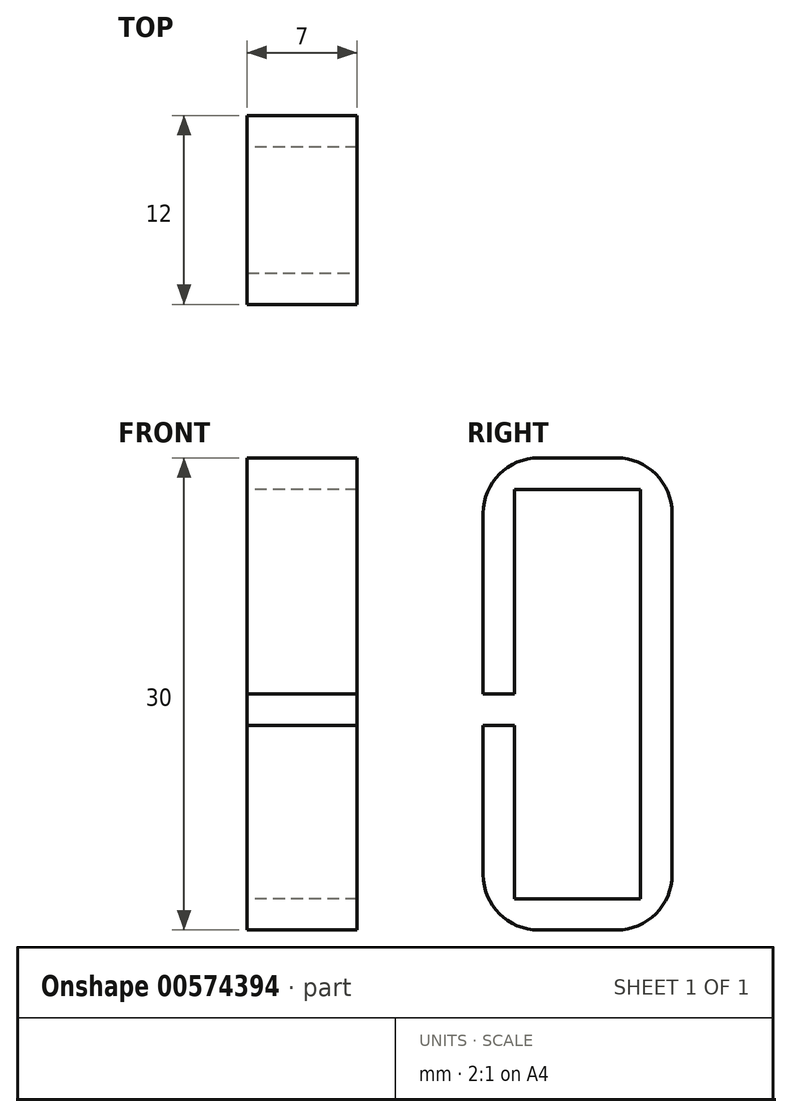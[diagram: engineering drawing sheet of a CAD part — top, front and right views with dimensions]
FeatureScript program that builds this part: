
annotation { "Feature Type Name" : "Feature", "Feature Type Description" : "" }
export const myFeature = defineFeature(function(context is Context, id is Id, definition is map)
    precondition{}
    {
        {
            var Q0;
            Q0=qCreatedBy(makeId("Front.planeOp"),FACE);
            var sketch = newSketch(context, id + "F0", { "sketchPlane" : qUnion([Q0])});
            skLineSegment(sketch, "E0.bottom", {"start": v(0, 0) * mm, "end": v(-7, 0) * mm});
            skLineSegment(sketch, "E0.top", {"start": v(0, 26) * mm, "end": v(-7, 26) * mm});
            skLineSegment(sketch, "E0.left", {"start": v(0, 0) * mm, "end": v(0, 26) * mm});
            skLineSegment(sketch, "E0.right", {"start": v(-7, 0) * mm, "end": v(-7, 26) * mm});
            skSolve(sketch);
        }
        {
            var Q0;
            Q0 = qSketchRegion(id + "F0", true);
            extrude(context, id + "F1", {"entities" : qUnion([Q0]), "depth" : 2 * mm, "offsetDistance" : 25.4 * mm});
        }
        {
            var Q0;
            Q0 = qSketchRegion(id + "F0", true);
            extrude(context, id + "F2", {"entities" : qUnion([Q0]), "depth" : 12 * mm, "offsetDistance" : 25.4 * mm, "hasSecondDirection" : true, "secondDirectionOppositeDirection" : false, "secondDirectionDepth" : 10 * mm});
        }
        {
            var Q0;
            Q0=makeQuery(id+"F1.opExtrude","SWEPT_FACE",FACE,{"disambiguationData":[OSD([sQuery(id+"F0.wireOp",EDGE,"E0.top")])]});
            var sketch = newSketch(context, id + "F3", { "sketchPlane" : qUnion([Q0])});
            skLineSegment(sketch, "E1.bottom", {"start": v(0, 0) * mm, "end": v(-7, 0) * mm});
            skLineSegment(sketch, "E1.top", {"start": v(0, -12) * mm, "end": v(-7, -12) * mm});
            skLineSegment(sketch, "E1.left", {"start": v(0, 0) * mm, "end": v(0, -12) * mm});
            skLineSegment(sketch, "E1.right", {"start": v(-7, 0) * mm, "end": v(-7, -12) * mm});
            skSolve(sketch);
        }
        {
            var Q0;
            Q0 = qSketchRegion(id + "F3", true);
            extrude(context, id + "F4", {"entities" : qUnion([Q0]), "depth" : 2 * mm, "offsetDistance" : 25.4 * mm});
        }
        {
            var Q0;
            Q0 = qSketchRegion(id + "F3", true);
            extrude(context, id + "F5", {"entities" : qUnion([Q0]), "oppositeDirection" : true, "depth" : 28 * mm, "offsetDistance" : 25.4 * mm, "hasSecondDirection" : true, "secondDirectionOppositeDirection" : true, "secondDirectionDepth" : 26 * mm});
        }
        {
            var Q0;
            Q0=makeQuery(id+"F1.opExtrude","SWEPT_BODY",BODY,{"disambiguationData":[OSD([sQuery(id+"F0.wireOp",EDGE,"E0.bottom"),sQuery(id+"F0.wireOp",EDGE,"E0.top"),sQuery(id+"F0.wireOp",EDGE,"E0.left"),sQuery(id+"F0.wireOp",EDGE,"E0.right")])]});
            var Q1;
            Q1=makeQuery(id+"F2.opExtrude","SWEPT_BODY",BODY,{"disambiguationData":[OSD([sQuery(id+"F0.wireOp",EDGE,"E0.bottom"),sQuery(id+"F0.wireOp",EDGE,"E0.top"),sQuery(id+"F0.wireOp",EDGE,"E0.left"),sQuery(id+"F0.wireOp",EDGE,"E0.right")])]});
            var Q2;
            Q2=makeQuery(id+"F4.opExtrude","SWEPT_BODY",BODY,{"disambiguationData":[OSD([sQuery(id+"F3.wireOp",EDGE,"E1.bottom"),sQuery(id+"F3.wireOp",EDGE,"E1.top"),sQuery(id+"F3.wireOp",EDGE,"E1.left"),sQuery(id+"F3.wireOp",EDGE,"E1.right")])]});
            var Q3;
            Q3=makeQuery(id+"F5.opExtrude","SWEPT_BODY",BODY,{"disambiguationData":[OSD([sQuery(id+"F3.wireOp",EDGE,"E1.bottom"),sQuery(id+"F3.wireOp",EDGE,"E1.top"),sQuery(id+"F3.wireOp",EDGE,"E1.left"),sQuery(id+"F3.wireOp",EDGE,"E1.right")])]});
            booleanBodies(context, id + "F6", {"operationType" : BooleanOperationType.UNION, "tools" : qUnion([Q0, Q1, Q2, Q3])});
        }
        {
            var Q0;
            {var subQ0=sQuery(id+"F3.wireOp",EDGE,"E1.top");Q0=makeQuery(id+"F6.opBoolean","MERGE",FACE,{"derivedFrom":[makeQuery(id+"F2.opExtrude","CAP_FACE",FACE,{"disambiguationData":[OSD([sQuery(id+"F0.wireOp",EDGE,"E0.bottom"),sQuery(id+"F0.wireOp",EDGE,"E0.top"),sQuery(id+"F0.wireOp",EDGE,"E0.left"),sQuery(id+"F0.wireOp",EDGE,"E0.right")])],"isStart":false}),makeQuery(id+"F4.opExtrude","SWEPT_FACE",FACE,{"disambiguationData":[OSD([subQ0])]}),makeQuery(id+"F5.opExtrude","SWEPT_FACE",FACE,{"disambiguationData":[OSD([subQ0])]})]});}
            var sketch = newSketch(context, id + "F7", { "sketchPlane" : qUnion([Q0])});
            skLineSegment(sketch, "E2", {"start": v(-7, 13) * mm, "end": v(0, 13) * mm});
            skLineSegment(sketch, "E3.top", {"start": v(-7, 11) * mm, "end": v(0, 11) * mm});
            skSolve(sketch);
        }
        {
            var Q0;
            {var subQ0=sQuery(id+"F7.wireOp",EDGE,"E2");Q0=makeQuery(id+"F7.imprint","IMPRINT",FACE,{"disambiguationData":[TD([[makeQuery(id+"F7.imprint","IMPRINT",EDGE,{"derivedFrom":subQ0}),-1.0]])]});}
            extrude(context, id + "F8", {"entities" : qUnion([Q0]), "operationType" : NewBodyOperationType.REMOVE, "oppositeDirection" : true, "depth" : 4 * mm, "offsetDistance" : 25.4 * mm});
        }
        {
            var Q0;
            Q0=makeQuery(id+"F4.opExtrude","CAP_EDGE",EDGE,{"disambiguationData":[OSD([sQuery(id+"F3.wireOp",EDGE,"E1.top")])],"isStart":false});
            var Q1;
            Q1=makeQuery(id+"F4.opExtrude","CAP_EDGE",EDGE,{"disambiguationData":[OSD([sQuery(id+"F3.wireOp",EDGE,"E1.bottom")])],"isStart":false});
            var Q2;
            Q2=makeQuery(id+"F5.opExtrude","CAP_EDGE",EDGE,{"disambiguationData":[OSD([sQuery(id+"F3.wireOp",EDGE,"E1.top")])],"isStart":false});
            var Q3;
            Q3=makeQuery(id+"F5.opExtrude","CAP_EDGE",EDGE,{"disambiguationData":[OSD([sQuery(id+"F3.wireOp",EDGE,"E1.bottom")])],"isStart":false});
            var Q4;
            Q4=makeQuery(id+"F1.opExtrude","CAP_EDGE",EDGE,{"disambiguationData":[OSD([sQuery(id+"F0.wireOp",EDGE,"E0.top")])],"isStart":false});
            var Q5;
            Q5=makeQuery(id+"F1.opExtrude","CAP_EDGE",EDGE,{"disambiguationData":[OSD([sQuery(id+"F0.wireOp",EDGE,"E0.bottom")])],"isStart":false});
            var Q6;
            Q6=makeQuery(id+"F2.opExtrude","CAP_EDGE",EDGE,{"disambiguationData":[OSD([sQuery(id+"F0.wireOp",EDGE,"E0.bottom")])],"isStart":true});
            var Q7;
            Q7=makeQuery(id+"F2.opExtrude","CAP_EDGE",EDGE,{"disambiguationData":[OSD([sQuery(id+"F0.wireOp",EDGE,"E0.top")])],"isStart":true});
            fillet(context, id + "F9", {"entities" : qUnion([Q0, Q1, Q2, Q3, Q4, Q5, Q6, Q7]), "radius" : 3.53 * mm, "tangentPropagation" : true, "allowEdgeOverflow" : false});
        }
    });
